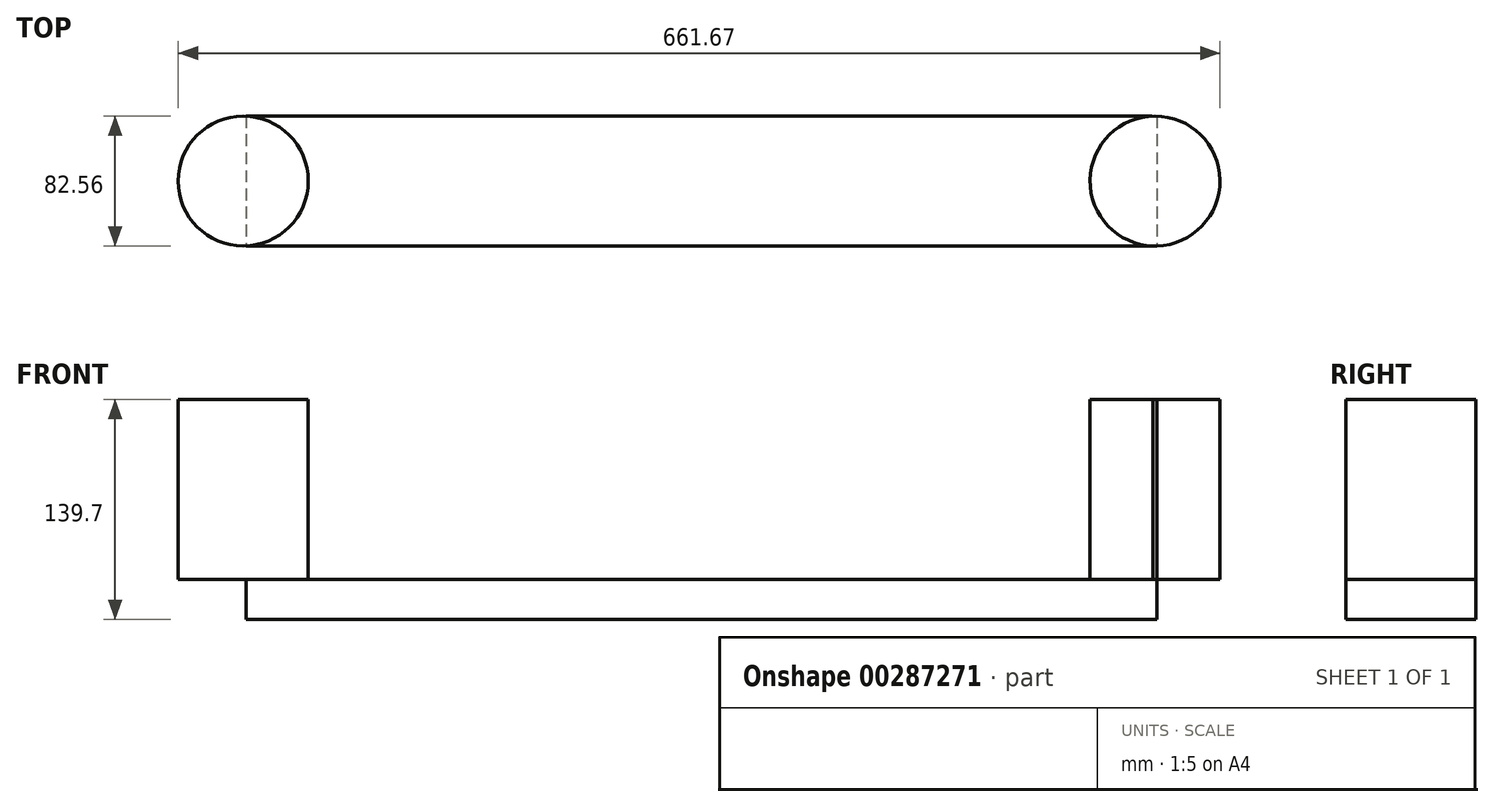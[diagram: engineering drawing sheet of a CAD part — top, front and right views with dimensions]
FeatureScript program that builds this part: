
annotation { "Feature Type Name" : "Feature", "Feature Type Description" : "" }
export const myFeature = defineFeature(function(context is Context, id is Id, definition is map)
    precondition{}
    {
        {
            var Q0;
            Q0=qCreatedBy(makeId("Top.planeOp"),FACE);
            var sketch = newSketch(context, id + "F0", { "sketchPlane" : qUnion([Q0])});
            skCircle(sketch, "E0", {"center": v(-219.73, 0) * mm, "radius": 41.28 * mm});
            skCircle(sketch, "E1", {"center": v(359.4, 0) * mm, "radius": 41.28 * mm});
            skLineSegment(sketch, "E2.bottom", {"start": v(-217.73, 41.23) * mm, "end": v(360.62, 41.23) * mm});
            skLineSegment(sketch, "E2.top", {"start": v(-217.73, -41.26) * mm, "end": v(360.62, -41.26) * mm});
            skLineSegment(sketch, "E2.left", {"start": v(-217.73, 41.23) * mm, "end": v(-217.73, -41.26) * mm});
            skLineSegment(sketch, "E2.right", {"start": v(360.62, 41.23) * mm, "end": v(360.62, -41.26) * mm});
            skSolve(sketch);
        }
        {
            var Q0;
            {var subQ0=sQuery(id+"F0.wireOp",EDGE,"E2.right");Q0=makeQuery(id+"F0.imprint","IMPRINT",FACE,{"disambiguationData":[TD([[makeQuery(id+"F0.imprint","IMPRINT",EDGE,{"derivedFrom":subQ0}),1.0]])]});}
            var Q1;
            {var subQ5=sQuery(id+"F0.wireOp",EDGE,"E2.right");Q1=makeQuery(id+"F0.imprint","IMPRINT",FACE,{"disambiguationData":[TD([[makeQuery(id+"F0.imprint","IMPRINT",EDGE,{"derivedFrom":subQ5}),-1.0]])]});}
            var Q2;
            {var subQ0=sQuery(id+"F0.wireOp",EDGE,"E2.left");var subQ1=sQuery(id+"F0.wireOp",EDGE,"E0");var subQ3=makeQuery(id+"F0.imprint","INTERSECT",VERTEX,{"derivedFrom":[subQ1,subQ0]});Q2=makeQuery(id+"F0.imprint","IMPRINT",FACE,{"disambiguationData":[TD([[makeQuery(id+"F0.imprint","IMPRINT",EDGE,{"disambiguationData":[TD([[subQ3,-1.0]])],"derivedFrom":subQ1}),1.0]])]});}
            var Q3;
            {var subQ0=sQuery(id+"F0.wireOp",EDGE,"E2.left");var subQ1=sQuery(id+"F0.wireOp",EDGE,"E0");var subQ3=makeQuery(id+"F0.imprint","INTERSECT",VERTEX,{"derivedFrom":[subQ1,subQ0]});Q3=makeQuery(id+"F0.imprint","IMPRINT",FACE,{"disambiguationData":[TD([[makeQuery(id+"F0.imprint","IMPRINT",EDGE,{"disambiguationData":[TD([[subQ3,1.0]])],"derivedFrom":subQ1}),1.0]])]});}
            extrude(context, id + "F1", {"entities" : qUnion([Q0, Q1, Q2, Q3]), "depth" : 114.3 * mm});
        }
        {
            var Q0;
            {var subQ4=sQuery(id+"F0.wireOp",EDGE,"E1");var subQ6=sQuery(id+"F0.wireOp",EDGE,"E2.top");var subQ8=makeQuery(id+"F0.imprint","INTERSECT",VERTEX,{"derivedFrom":[subQ4,subQ6]});Q0=makeQuery(id+"F0.imprint","IMPRINT",FACE,{"disambiguationData":[TD([[makeQuery(id+"F0.imprint","IMPRINT",EDGE,{"disambiguationData":[TD([[subQ8,1.0]])],"derivedFrom":subQ4}),-1.0]])]});}
            var Q1;
            {var subQ0=sQuery(id+"F0.wireOp",EDGE,"E2.left");var subQ1=sQuery(id+"F0.wireOp",EDGE,"E0");var subQ3=makeQuery(id+"F0.imprint","INTERSECT",VERTEX,{"derivedFrom":[subQ1,subQ0]});Q1=makeQuery(id+"F0.imprint","IMPRINT",FACE,{"disambiguationData":[TD([[makeQuery(id+"F0.imprint","IMPRINT",EDGE,{"disambiguationData":[TD([[subQ3,-1.0]])],"derivedFrom":subQ1}),1.0]])]});}
            var Q2;
            {var subQ5=sQuery(id+"F0.wireOp",EDGE,"E2.right");Q2=makeQuery(id+"F0.imprint","IMPRINT",FACE,{"disambiguationData":[TD([[makeQuery(id+"F0.imprint","IMPRINT",EDGE,{"derivedFrom":subQ5}),-1.0]])]});}
            extrude(context, id + "F2", {"entities" : qUnion([Q0, Q1, Q2]), "oppositeDirection" : true, "depth" : 25.4 * mm});
        }
    });
